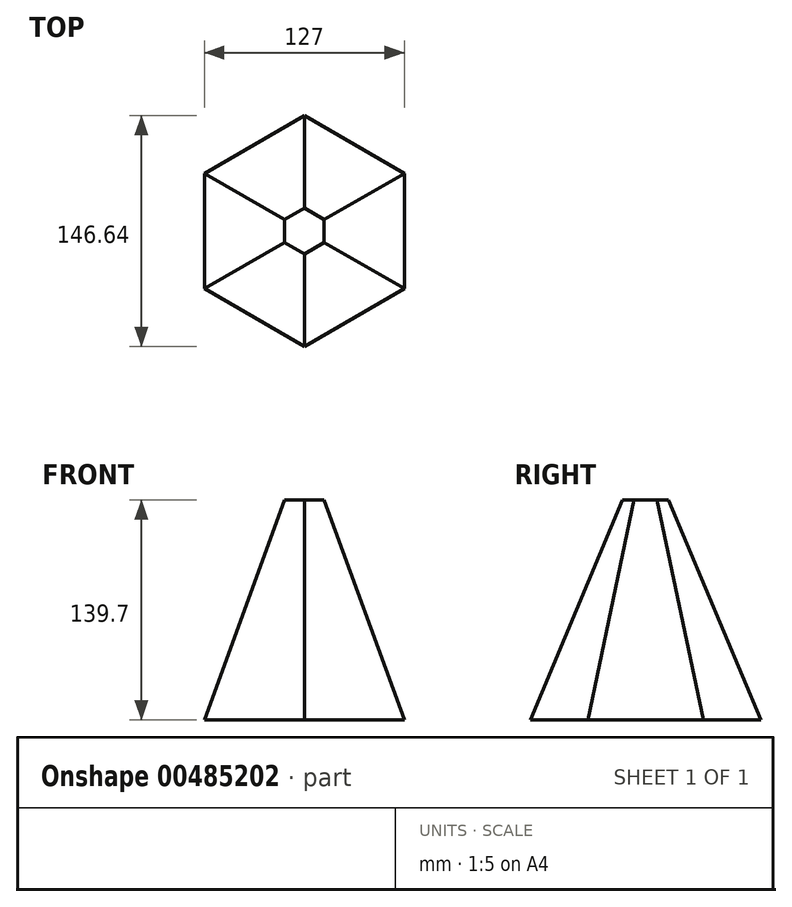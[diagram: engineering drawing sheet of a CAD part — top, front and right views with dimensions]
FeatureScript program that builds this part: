
annotation { "Feature Type Name" : "Feature", "Feature Type Description" : "" }
export const myFeature = defineFeature(function(context is Context, id is Id, definition is map)
    precondition{}
    {
        {
            var Q0;
            Q0=qCreatedBy(makeId("Top.planeOp"),FACE);
            var sketch = newSketch(context, id + "F0", { "sketchPlane" : qUnion([Q0])});
            skCircle(sketch, "E0.cCircle", {"center": v(0, 0) * mm, "radius": 63.5 * mm, "construction": true});
            skLineSegment(sketch, "E0.0", {"start": v(63.5, 36.66) * mm, "end": v(63.5, -36.66) * mm});
            skLineSegment(sketch, "E0.1", {"start": v(63.5, -36.66) * mm, "end": v(0, -73.32) * mm});
            skLineSegment(sketch, "E0.2", {"start": v(0, -73.32) * mm, "end": v(-63.5, -36.66) * mm});
            skLineSegment(sketch, "E0.3", {"start": v(-63.5, -36.66) * mm, "end": v(-63.5, 36.66) * mm});
            skLineSegment(sketch, "E0.4", {"start": v(-63.5, 36.66) * mm, "end": v(0, 73.32) * mm});
            skLineSegment(sketch, "E0.5", {"start": v(0, 73.32) * mm, "end": v(63.5, 36.66) * mm});
            skPoint(sketch, "E0.0.midPoint", {"position": v(63.5, 0) * mm});
            skSolve(sketch);
        }
        {
            var Q0;
            Q0=makeQuery(id+"F0.imprint","IMPRINT",FACE,{"disambiguationData":[TD([[makeQuery(id+"F0.imprint","IMPRINT",EDGE,{"derivedFrom":sQuery(id+"F0.wireOp",EDGE,"E0.0")}),-1.0]])]});
            extrude(context, id + "F1", {"entities" : qUnion([Q0]), "depth" : 139.7 * mm, "hasDraft" : true, "draftAngle" : 20 * degree, "draftPullDirection" : true});
        }
    });
